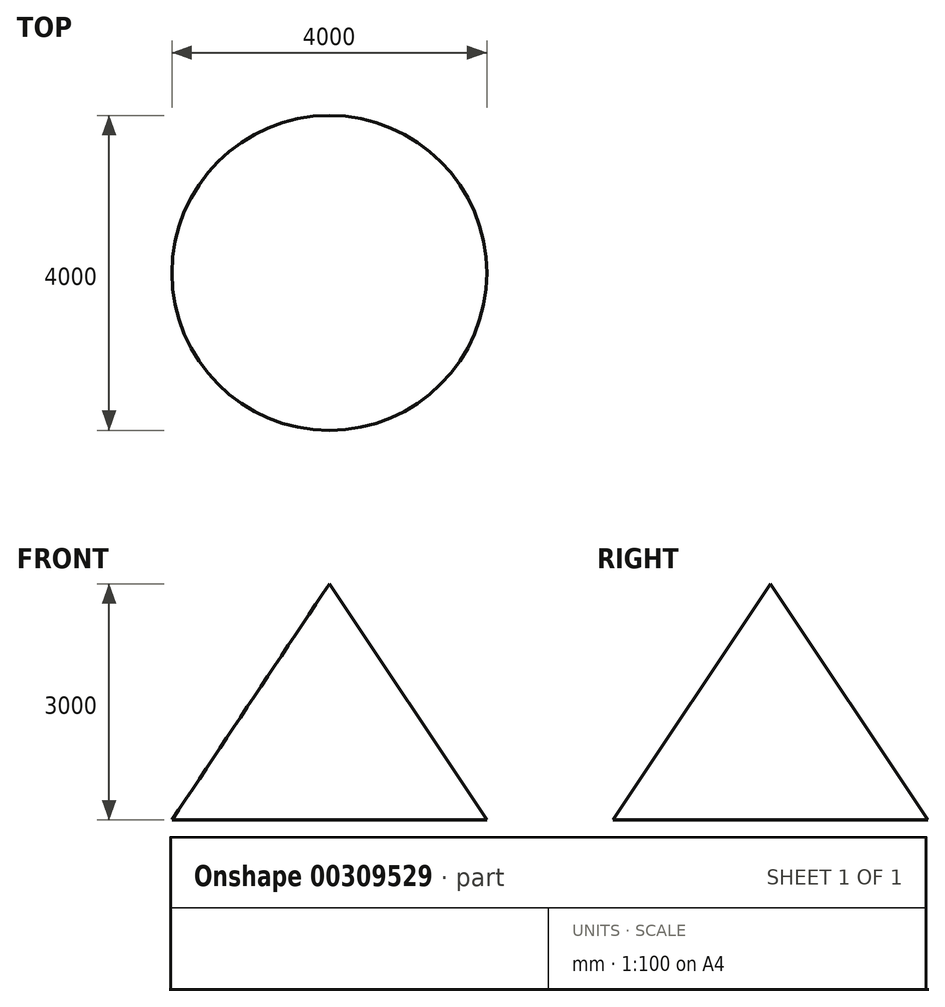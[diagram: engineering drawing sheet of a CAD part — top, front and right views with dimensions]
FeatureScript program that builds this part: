
annotation { "Feature Type Name" : "Feature", "Feature Type Description" : "" }
export const myFeature = defineFeature(function(context is Context, id is Id, definition is map)
    precondition{}
    {
        {
            var Q0;
            Q0=qCreatedBy(makeId("Front.planeOp"),FACE);
            var sketch = newSketch(context, id + "F0", { "sketchPlane" : qUnion([Q0])});
            skLineSegment(sketch, "E0", {"start": v(0, 0) * mm, "end": v(0, 3000) * mm});
            skLineSegment(sketch, "E1", {"start": v(0, 3000) * mm, "end": v(2000, 0) * mm});
            skLineSegment(sketch, "E2", {"start": v(2000, 0) * mm, "end": v(0, 0) * mm});
            skSolve(sketch);
        }
        {
            var Q0;
            Q0=makeQuery(id+"F0.imprint","IMPRINT",FACE,{"disambiguationData":[TD([[makeQuery(id+"F0.imprint","IMPRINT",EDGE,{"derivedFrom":sQuery(id+"F0.wireOp",EDGE,"E0")}),-1.0]])]});
            var Q1;
            Q1=sQuery(id+"F0.wireOp",EDGE,"E0");
            revolve(context, id + "F1", {"entities" : qUnion([Q0]), "axis" : qUnion([Q1]), "revolveType" : RevolveType.FULL});
        }
    });
